# Revit family: 1DIBI_PORTE_BLINDATE_DIBIG
name_source: partatom
category: Porte
revit_build: Autodesk Revit 2018 (Build: 20190510_1515(x64)
units: mm (PartAtom-declared; Revit-internal decimal feet)

## family parameters
Condiviso = No
Host = Muro
Numero OmniClass = 23.30.10.00
Punto di calcolo locali = No
Sempre verticale = Sì
Taglio con vuoti quando caricato = No
Titolo OmniClass = Doors

## types (2) — shared parameters
ABBATTIMENTO ACUSTICO = 38 dB
AUTORE BIM = https://bim.archiproducts.com
Altezza = 2200.00 mm
Altezza approssimativa = 2200.00 mm
BADGE BIM = https://bim.archiproducts.com
CLASSE DI SICUREZZA = Classe 4
Chiusura muro = Per host
Coefficiente di scambio termico (U) = 1.5000 W/(m²·K)
Costruzione analitica = <Nessuno>
Descrizione = Porta d'ingresso a bilico blindata
FINITURE DISPONIBILI = Per tutti i materiali e le finiture disponibili fare riferimento alla scheda tecnica sul sito del produttore.
Funzione = Interno
ISTRUZIONI INSTALLAZIONE = https://www.dibigroup.com
LUCE PASSAGGIO = 900.00 mm
Larghezza = 1200.00 mm
Larghezza approssimativa = 1200.00 mm
MANUALE UTENTE BIM = https://img.edilportale.com
MATERIALE MANIGLIE = Cromo lucido
Modello = DI.BIG
PERMEABILITA' ALL'ARIA = Classe 2
Produttore = DiBi Porte Blindate
RESISTENZA AL VENTO = Classe C5
RIVESTIMENTO ESTERNO = Rovere Naturale
RIVESTIMENTO INTERNO = Laccato RAL Perlato
SCHEDA PRODOTTO = https://www.archiproducts.com
SCHEDA TECNICA = https://www.dibigroup.com
Spessore = 95.00 mm
TENUTA ALL'ACQUA = Classe 4A
URL = https://www.dibigroup.com

## per-type parameters (varying)
| type | Profilo1 | Profilo2 | SPESSORE SGUINCIO |
| 120x220cm_SOLUZIONI_20-22 | Sì | No | 0.00 mm |
| 120x220cm_SOLUZIONI_21-23 | No | Sì | 12.00 mm |
